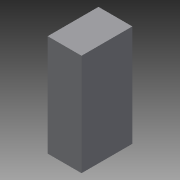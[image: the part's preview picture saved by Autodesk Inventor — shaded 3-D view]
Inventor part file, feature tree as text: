
AUTODESK INVENTOR PART (.ipt)
format: ipt  version: 2014 (Build 180170000, 170)  size: 67,584 bytes
history: native  units: in
note: dims shown in document units (in); Inventor stores cm internally (conversion verified against a paired STEP export)
features: extrude x1, sketch x1
ambient origin geometry x8: Origin, YZ Plane, XZ Plane, XY Plane, X Axis, Y Axis, Z Axis, Center Point
bodies: Solid1 (feature_tree)
feature tree (2):
  extrude  "Extrusion1"  Depth=36.0in
  sketch  "Sketch1"  dims[d0=24.0in d1=36.0in d2=72.0in d3=0.0in]
